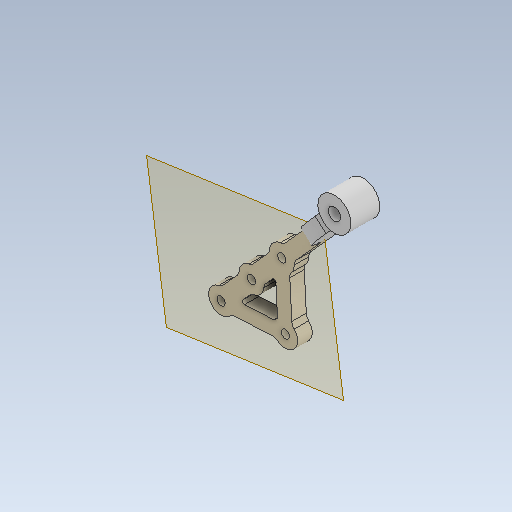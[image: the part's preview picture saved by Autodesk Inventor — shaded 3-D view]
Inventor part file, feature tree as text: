
AUTODESK INVENTOR PART (.ipt)
format: ipt  version: 2023 (Build 270158000, 158)  size: 231,424 bytes
history: native  units: mm
features: sketch x8, other x3, plane x1
ambient origin geometry x8: Origin, YZ Plane, XZ Plane, XY Plane, X Axis, Y Axis, Z Axis, Center Point
bodies: Solid1 (feature_tree)
feature tree (12):
  other  "leg_link_2.ipt"
  other  "Solid1::leg_link_2.ipt"
  other  "TaggingFeature1"
  sketch  "Sketch1"  dims[d0=10.0mm]
  sketch  "Sketch2"
  sketch  "Sketch3"
  sketch  "Sketch4"
  sketch  "Sketch5"
  sketch  "Sketch6"
  sketch  "Sketch7"
  sketch  "Sketch8"
  plane  "Work Plane1"
